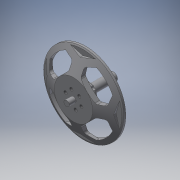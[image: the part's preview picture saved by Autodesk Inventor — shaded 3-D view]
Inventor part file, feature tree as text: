
AUTODESK INVENTOR PART (.ipt)
format: ipt  version: 2019.4 (Build 234330000, 330)  size: 351,232 bytes
history: native  units: mm
features: sketch x11, extrude x8, pattern_circular x3, fillet x2, hole x2, revolve x1, projected_geometry x1
ambient origin geometry x8: Origin, YZ Plane, XZ Plane, XY Plane, X Axis, Y Axis, Z Axis, Center Point
bodies: Solid1 (feature_tree)
feature tree (28):
  extrude  "Extrusion1"  Depth=9.0mm TaperAngle=0.0deg
  extrude  "Extrusion2"  Depth=28.0mm
  extrude  "Extrusion3"  Depth=7.5mm TaperAngle=0.0deg
  revolve  "Revolution1"  [1 undecoded]
  extrude  "Extrusion4"  Depth=40.0mm TaperAngle=360.0deg
  fillet  "Fillet1"  [1 undecoded]
  pattern_circular  "Circular Pattern1"  Count=4 Angle=360.0deg
  extrude  "Extrusion5"  Depth=4.2mm
  pattern_circular  "Circular Pattern2"  Count=4 Angle=360.0deg
  extrude  "Extrusion7"  Depth=2.0mm
  fillet  "Fillet2"  Radius=3.0mm
  hole  "Hole1"  [1 undecoded]
  pattern_circular  "Circular Pattern3"  [2 undecoded]
  extrude  "Extrusion6"  Depth=2.0mm TaperAngle=0.0deg
  extrude  "Extrusion8"  Depth=2.0mm
  hole  "Hole2"  [1 undecoded]
  sketch  "Sketch1"  dims[d0=58.6mm d1=9.0mm d2=0.0mm]
  sketch  "Sketch2"  dims[d3=3.7mm d4=28.0mm]
  sketch  "Sketch3"  dims[d5=3.7mm d6=0.0mm d7=7.5mm d8=0.0mm]
  projected_geometry  "Projected Loop1"
  sketch  "Sketch4"  dims[d9=90.0deg d10=8.6mm]
  sketch  "Sketch5"  dims[d11=4.3mm d12=40.0mm d14=360.0deg d16=45.0deg]
  sketch  "Sketch6"  dims[d18=16.5mm]
  sketch  "Sketch7"  dims[d19=7.5mm d20=0.0mm]
  sketch  "Sketch8"  dims[d21=2.0mm d22=40.0mm d23=360.0deg]
  sketch  "Sketch9"  dims[d25=4.2mm d26=4.2mm]
  sketch  "Sketch10"  dims[d27=7.0mm d28=0.0mm d29=40.0mm d30=360.0deg]
  sketch  "Sketch11"  dims[d32=45.0deg d33=6.0mm d34=3.0mm d35=2.459mm d36=10.0mm d37=4.34mm d38=2.0mm d39=1.22173mm d40=8.8mm d41=0.0mm d42=60.0mm d43=360.0deg d45=4.0mm d46=5.0mm d47=0.0mm d48=12.0mm d49=8.0mm d50=0.0mm d51=1.0mm d52=6.0mm d53=17.5mm d54=0.0mm d55=2.459mm d56=6.0mm d57=4.0mm d58=2.0mm d59=90.0deg d60=8.8mm d61=20.594885mm]
note: 6 required parameter values undecoded (feature->parameter linkage not recoverable at this tier; creation-order binding heuristic only, values carry confidence <= 0.55)